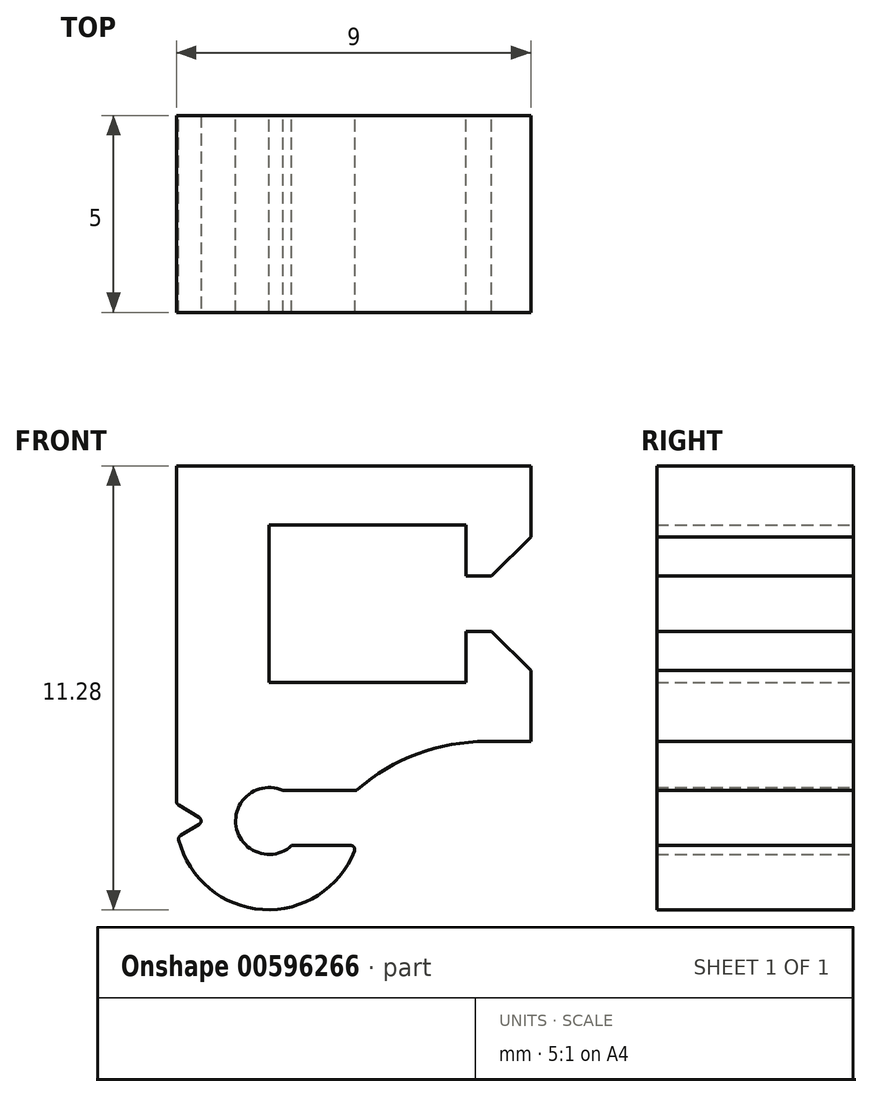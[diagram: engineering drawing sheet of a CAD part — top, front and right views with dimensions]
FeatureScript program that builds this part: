
annotation { "Feature Type Name" : "Feature", "Feature Type Description" : "" }
export const myFeature = defineFeature(function(context is Context, id is Id, definition is map)
    precondition{}
    {
        {
            var Q0;
            Q0=qCreatedBy(makeId("Front.planeOp"),FACE);
            var sketch = newSketch(context, id + "F0", { "sketchPlane" : qUnion([Q0])});
            skArc(sketch, "E0", {"start": v(0.35, 0.78) * mm, "mid": v(-0.84, -0.14) * mm, "end": v(0.58, -0.62) * mm});
            skLineSegment(sketch, "E1", {"start": v(0, 0) * mm, "end": v(2.86, 0) * mm, "construction": true});
            skLineSegment(sketch, "E2", {"start": v(0.35, 0.78) * mm, "end": v(2.22, 0.78) * mm});
            skLineSegment(sketch, "E3", {"start": v(0.58, -0.62) * mm, "end": v(2.22, -0.62) * mm});
            skPoint(sketch, "E4.orphan", {"position": v(0, 0.78) * mm});
            skPoint(sketch, "E5.orphan", {"position": v(0, -0.62) * mm});
            skLineSegment(sketch, "E6", {"start": v(-2.35, 0.43) * mm, "end": v(-2.35, 9.02) * mm});
            skLineSegment(sketch, "E7", {"start": v(-2.35, 9.02) * mm, "end": v(6.65, 9.02) * mm});
            skLineSegment(sketch, "E8", {"start": v(6.65, 9.02) * mm, "end": v(6.65, 6.22) * mm});
            skLineSegment(sketch, "E9", {"start": v(6.65, 6.22) * mm, "end": v(5, 6.22) * mm});
            skLineSegment(sketch, "E10", {"start": v(5, 6.22) * mm, "end": v(5, 7.52) * mm});
            skLineSegment(sketch, "E11", {"start": v(5, 7.52) * mm, "end": v(0, 7.52) * mm});
            skLineSegment(sketch, "E12", {"start": v(0, 7.52) * mm, "end": v(0, 3.52) * mm});
            skLineSegment(sketch, "E13", {"start": v(0, 3.52) * mm, "end": v(5, 3.52) * mm});
            skLineSegment(sketch, "E14", {"start": v(5, 3.52) * mm, "end": v(5, 4.82) * mm});
            skLineSegment(sketch, "E15", {"start": v(5, 4.82) * mm, "end": v(6.65, 4.82) * mm});
            skLineSegment(sketch, "E16", {"start": v(6.65, 4.82) * mm, "end": v(6.65, 2.02) * mm});
            skLineSegment(sketch, "E17", {"start": v(6.65, 2.02) * mm, "end": v(2.22, 2.02) * mm});
            skLineSegment(sketch, "E18", {"start": v(2.22, 0.78) * mm, "end": v(2.22, 2.02) * mm});
            skArc(sketch, "E19.trimOffspring", {"start": v(-2.31, -0.41) * mm, "mid": v(-0.13, -2.25) * mm, "end": v(2.22, -0.62) * mm});
            skLineSegment(sketch, "E20", {"start": v(-2.35, 0.43) * mm, "end": v(-1.64, 0) * mm});
            skLineSegment(sketch, "E21", {"start": v(-1.64, 0) * mm, "end": v(-2.31, -0.41) * mm});
            skSolve(sketch);
        }
        {
            var Q0;
            Q0=makeQuery(id+"F0.imprint","IMPRINT",FACE,{"disambiguationData":[TD([[makeQuery(id+"F0.imprint","IMPRINT",EDGE,{"derivedFrom":sQuery(id+"F0.wireOp",EDGE,"E0")}),-1.0]])]});
            extrude(context, id + "F1", {"entities" : qUnion([Q0]), "depth" : 5 * mm, "offsetDistance" : 25 * mm});
        }
        {
            var Q0;
            Q0=makeQuery(id+"F1.opExtrude","SWEPT_EDGE",EDGE,{"disambiguationData":[OSD([sQuery(id+"F0.wireOp",EDGE,"E8"),sQuery(id+"F0.wireOp",EDGE,"E9")])]});
            var Q1;
            Q1=makeQuery(id+"F1.opExtrude","SWEPT_EDGE",EDGE,{"disambiguationData":[OSD([sQuery(id+"F0.wireOp",EDGE,"E15"),sQuery(id+"F0.wireOp",EDGE,"E16")])]});
            chamfer(context, id + "F2", {"entities" : qUnion([Q0, Q1]), "width" : 1 * mm, "tangentPropagation" : true});
        }
        {
            var Q0;
            Q0=makeQuery(id+"F1.opExtrude","SWEPT_EDGE",EDGE,{"disambiguationData":[OSD([sQuery(id+"F0.wireOp",EDGE,"E17"),sQuery(id+"F0.wireOp",EDGE,"E18")])]});
            fillet(context, id + "F3", {"entities" : qUnion([Q0]), "radius" : 5 * mm, "tangentPropagation" : true, "allowEdgeOverflow" : false});
        }
        {
            var Q0;
            Q0=makeQuery(id+"F1.opExtrude","SWEPT_EDGE",EDGE,{"disambiguationData":[OSD([sQuery(id+"F0.wireOp",EDGE,"E20"),sQuery(id+"F0.wireOp",EDGE,"E21")])]});
            var Q1;
            Q1=makeQuery(id+"F1.opExtrude","SWEPT_EDGE",EDGE,{"disambiguationData":[OSD([sQuery(id+"F0.wireOp",EDGE,"E19.trimOffspring"),sQuery(id+"F0.wireOp",EDGE,"E21")])]});
            var Q2;
            Q2=makeQuery(id+"F1.opExtrude","SWEPT_EDGE",EDGE,{"disambiguationData":[OSD([sQuery(id+"F0.wireOp",EDGE,"E6"),sQuery(id+"F0.wireOp",EDGE,"E20")])]});
            var Q3;
            Q3=makeQuery(id+"F1.opExtrude","SWEPT_EDGE",EDGE,{"disambiguationData":[OSD([sQuery(id+"F0.wireOp",EDGE,"E3"),sQuery(id+"F0.wireOp",EDGE,"E19.trimOffspring")])]});
            var Q4;
            Q4=makeQuery(id+"F3.opFillet","BLEND_EDGE",EDGE,{"blendedFrom":[makeQuery(id+"F1.opExtrude","SWEPT_EDGE",EDGE,{"disambiguationData":[OSD([sQuery(id+"F0.wireOp",EDGE,"E17"),sQuery(id+"F0.wireOp",EDGE,"E18")])]}),makeQuery(id+"F1.opExtrude","SWEPT_FACE",FACE,{"disambiguationData":[OSD([sQuery(id+"F0.wireOp",EDGE,"E2")])]})],"blendedInto":[makeQuery(id+"F1.opExtrude","SWEPT_FACE",FACE,{"disambiguationData":[OSD([sQuery(id+"F0.wireOp",EDGE,"E2")])]})]});
            fillet(context, id + "F4", {"entities" : qUnion([Q0, Q1, Q2, Q3, Q4]), "radius" : 0.1 * mm, "tangentPropagation" : true, "allowEdgeOverflow" : false});
        }
    });
